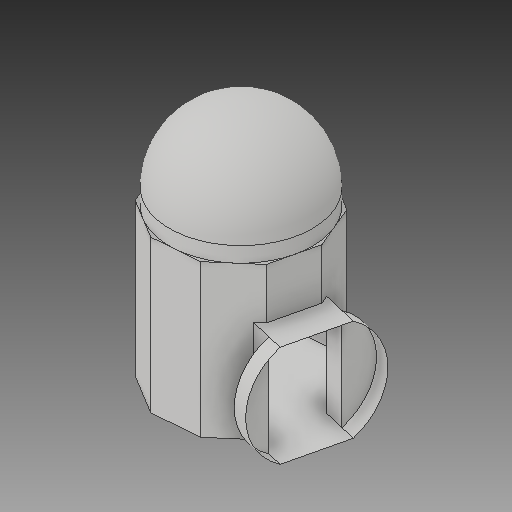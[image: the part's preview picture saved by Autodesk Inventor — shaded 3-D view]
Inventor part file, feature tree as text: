
AUTODESK INVENTOR PART (.ipt)
format: ipt  version: 2017 (Build 210142000, 142)  size: 285,696 bytes
history: native  units: in
note: dims shown in document units (in); Inventor stores cm internally (conversion verified against a paired STEP export)
features: sketch x7, extrude x6, other x2, delete_face x1
ambient origin geometry x8: Origin, YZ Plane, XZ Plane, XY Plane, X Axis, Y Axis, Z Axis, Center Point
bodies: Solid1 (feature_tree)
feature tree (16):
  extrude  "bace"  Depth=1.0in TaperAngle=0.0deg
  extrude  "bace wall"  Depth=10.0in TaperAngle=0.0deg
  extrude  "bace cieiling"  Depth=6.6667in
  other  "dome work plane"
  other  "dome"
  extrude  "door frame"  Depth=4.6918in
  sketch  "Sketch7"  dims[d18=1.6875in d19=0.0in d32=4.6918in]
  extrude  "corridor connection"  TaperAngle=90.0deg  [1 undecoded]
  extrude  "hide sliding doors"  Depth=1.0in TaperAngle=0.0deg
  delete_face  "Delete Face2"
  sketch  "Sketch1"  dims[d0=11.3835in d1=1.0in d2=0.0in]
  sketch  "Sketch2"  dims[d4=1.0in d5=10.0in d6=0.0in]
  sketch  "Sketch3"  dims[d8=1.0in d9=0.0in d16=2.0in d17=6.6667in]
  sketch  "Sketch8"  dims[d33=5.6918in d34=90.0deg]
  sketch  "Sketch10"  dims[d38=1.0in d42=1.2585in d43=0.0in]
  sketch  "Sketch11"  dims[d79=4.0in d81=3.8873in d82=3.8873in d86=1.6458in d91=3.3333in d92=1.0in d93=1.0in d95=1.0in d96=0.0in]
note: 1 required parameter value undecoded (feature->parameter linkage not recoverable at this tier; creation-order binding heuristic only, values carry confidence <= 0.55)
